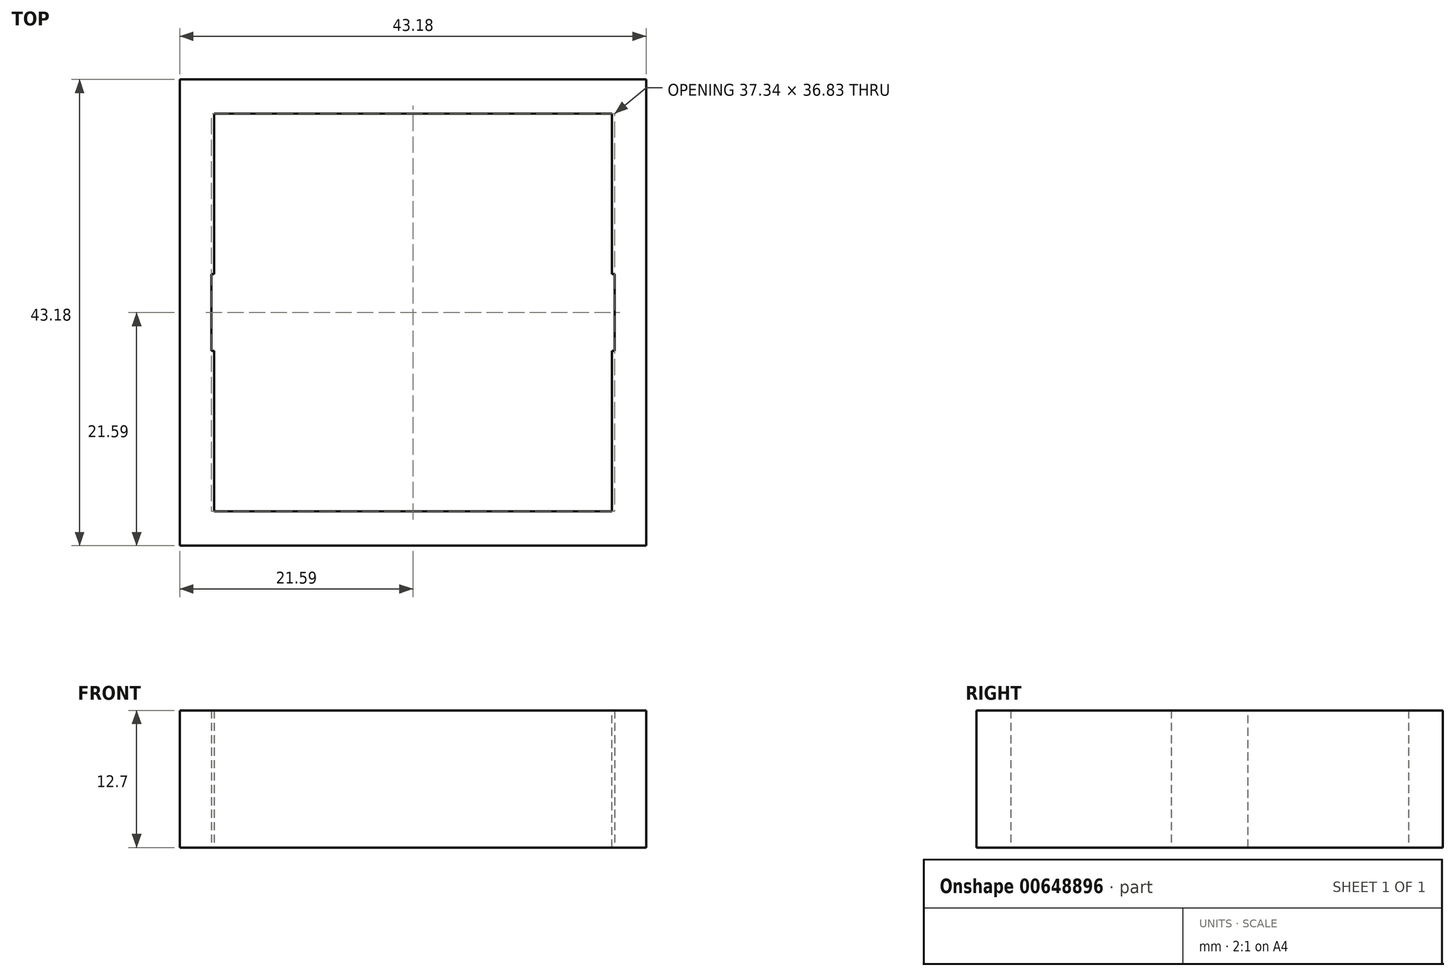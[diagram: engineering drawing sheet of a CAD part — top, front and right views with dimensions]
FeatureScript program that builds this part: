
annotation { "Feature Type Name" : "Feature", "Feature Type Description" : "" }
export const myFeature = defineFeature(function(context is Context, id is Id, definition is map)
    precondition{}
    {
        {
            var Q0;
            Q0=qCreatedBy(makeId("Top.planeOp"),FACE);
            var sketch = newSketch(context, id + "F0", { "sketchPlane" : qUnion([Q0])});
            skLineSegment(sketch, "E0.bottom", {"start": v(21.6, -21.59) * mm, "end": v(-21.59, -21.6) * mm});
            skLineSegment(sketch, "E0.top", {"start": v(21.59, 21.59) * mm, "end": v(-21.6, 21.59) * mm});
            skLineSegment(sketch, "E0.left", {"start": v(21.6, -21.59) * mm, "end": v(21.59, 21.59) * mm});
            skLineSegment(sketch, "E0.right", {"start": v(-21.59, -21.6) * mm, "end": v(-21.6, 21.59) * mm});
            skPoint(sketch, "E0.middle", {"position": v(0, 0) * mm});
            skLineSegment(sketch, "E1.bottom", {"start": v(18.42, 18.42) * mm, "end": v(-18.42, 18.41) * mm});
            skLineSegment(sketch, "E1.top", {"start": v(18.41, -18.41) * mm, "end": v(-18.41, -18.42) * mm});
            skLineSegment(sketch, "E1.left", {"start": v(-18.41, -18.42) * mm, "end": v(-18.41, 18.42) * mm});
            skLineSegment(sketch, "E1.right", {"start": v(18.41, -18.42) * mm, "end": v(18.41, 18.42) * mm});
            skSolve(sketch);
        }
        {
            var Q0;
            Q0 = qSketchRegion(id + "F0", true);
            extrude(context, id + "F1", {"entities" : qUnion([Q0]), "depth" : 12.7 * mm, "offsetDistance" : 25.4 * mm});
        }
        {
            var Q0;
            Q0=makeQuery(id+"F1.opExtrude","CAP_FACE",FACE,{"disambiguationData":[OSD([sQuery(id+"F0.wireOp",EDGE,"E0.bottom"),sQuery(id+"F0.wireOp",EDGE,"E0.top"),sQuery(id+"F0.wireOp",EDGE,"E0.left"),sQuery(id+"F0.wireOp",EDGE,"E0.right"),sQuery(id+"F0.wireOp",EDGE,"E1.bottom"),sQuery(id+"F0.wireOp",EDGE,"E1.top"),sQuery(id+"F0.wireOp",EDGE,"E1.left"),sQuery(id+"F0.wireOp",EDGE,"E1.right")])],"isStart":true});
            var sketch = newSketch(context, id + "F2", { "sketchPlane" : qUnion([Q0])});
            skLineSegment(sketch, "E2.bottom", {"start": v(18.67, -3.56) * mm, "end": v(18.16, -3.56) * mm});
            skLineSegment(sketch, "E2.top", {"start": v(18.67, 3.56) * mm, "end": v(18.16, 3.56) * mm});
            skLineSegment(sketch, "E2.left", {"start": v(18.67, -3.56) * mm, "end": v(18.67, 3.56) * mm});
            skLineSegment(sketch, "E2.right", {"start": v(18.16, -3.56) * mm, "end": v(18.16, 3.56) * mm});
            skPoint(sketch, "E2.middle", {"position": v(18.41, 0) * mm});
            skLineSegment(sketch, "E3.bottom", {"start": v(-18.67, 3.56) * mm, "end": v(-18.16, 3.56) * mm});
            skLineSegment(sketch, "E3.top", {"start": v(-18.67, -3.56) * mm, "end": v(-18.16, -3.56) * mm});
            skLineSegment(sketch, "E3.left", {"start": v(-18.67, 3.56) * mm, "end": v(-18.67, -3.56) * mm});
            skLineSegment(sketch, "E3.right", {"start": v(-18.16, 3.56) * mm, "end": v(-18.16, -3.56) * mm});
            skPoint(sketch, "E3.middle", {"position": v(-18.41, 0) * mm});
            skSolve(sketch);
        }
        {
            var Q0;
            Q0 = qSketchRegion(id + "F2", true);
            extrude(context, id + "F3", {"entities" : qUnion([Q0]), "operationType" : NewBodyOperationType.REMOVE, "endBound" : BoundingType.THROUGH_ALL, "oppositeDirection" : true, "depth" : 21.59 * mm, "offsetDistance" : 25.4 * mm});
        }
    });
